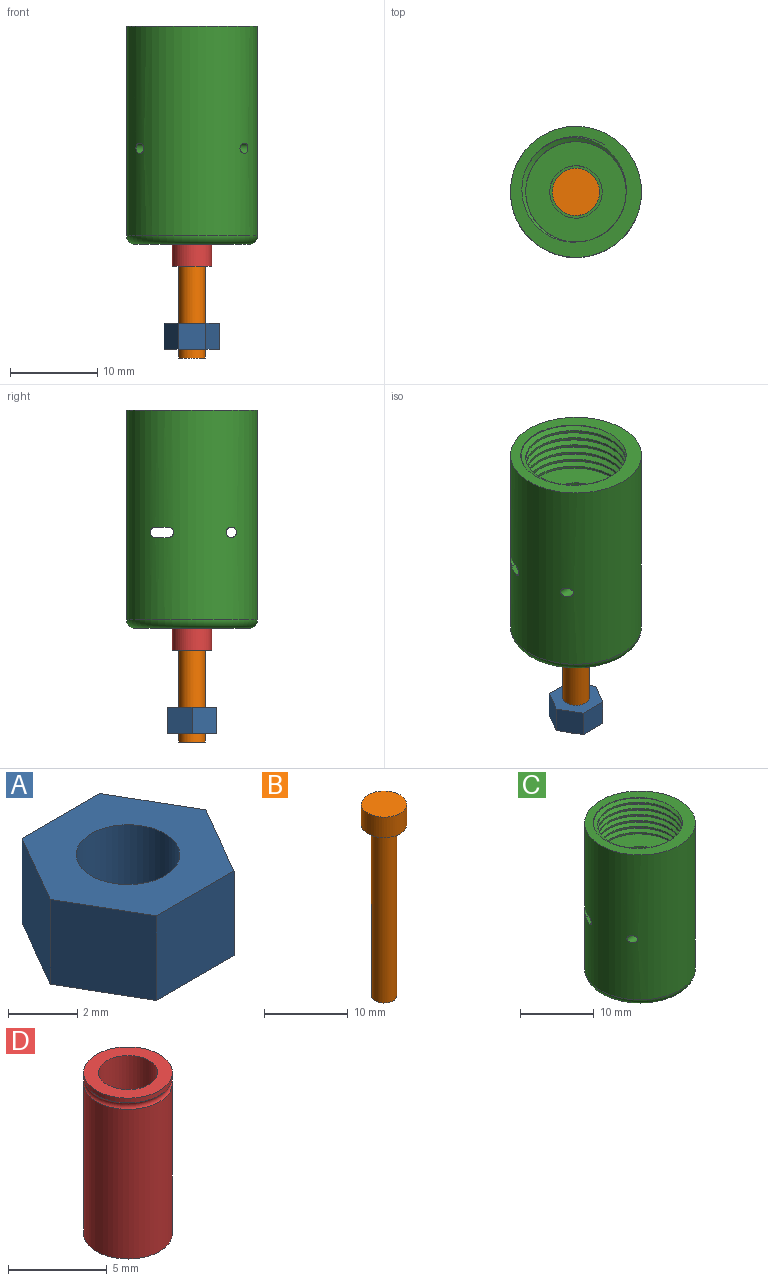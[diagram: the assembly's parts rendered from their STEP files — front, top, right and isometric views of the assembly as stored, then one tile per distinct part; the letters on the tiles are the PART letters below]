
ASSEMBLY  parts=4 mates=3
PART A: 9 faces, bbox 6.4x5.5x3 mm
  f0: plane 3x2.75mm, normal (0.87,0.5,0), area 9.5mm2, adj f1,f6,f7,f8
  f1: plane 3.18x3mm, normal (0,1,0), area 9.5mm2, adj f0,f2,f7,f8
  f2: plane 3x2.75mm, normal (-0.87,0.5,0), area 9.5mm2, adj f1,f3,f7,f8
  f3: plane 3x2.75mm, normal (-0.87,-0.5,0), area 9.5mm2, adj f2,f4,f7,f8
  f4: plane 3.18x3mm, normal (0,-1,0), area 9.5mm2, adj f3,f6,f7,f8
  f5: cylinder r=1.5mm len=3mm, axis (0,0,-1), area 28.3mm2, adj f7,f8
  f6: plane 3x2.75mm, normal (0.87,-0.5,0), area 9.5mm2, adj f0,f4,f7,f8
  f7: plane 6.35x5.5mm, normal (0,0,1), area 19.1mm2, adj f0,f1,f2,f3,f4,f5,f6
  f8: plane 6.35x5.5mm, normal (0,0,-1), area 19.1mm2, adj f0,f1,f2,f3,f4,f5,f6
PART B: 5 faces, bbox 5.4x5.4x28 mm
  f0: cylinder r=2.7mm len=5.4mm, axis (0,0,1), area 50.9mm2, adj f1,f2
  f1: plane 5.4x5.4mm, normal (0,0,-1), area 15.8mm2, adj f0,f3
  f2: plane 5.4x5.4mm, normal (0,0,1), area 22.9mm2, adj f0
  f3: cylinder r=1.5mm len=25mm, axis (0,0,1), area 235.6mm2, adj f1,f4
  f4: plane 3x3mm, normal (0,0,-1), area 7.1mm2, adj f3
PART C: 21 faces, bbox 16.6x16.6x25.7 mm
  f0: cylinder r=7.5mm len=24mm, axis (0,0,-1), area 1121.5mm2, adj f3,f12,f16,f17,f18,f19,f20
  f1: plane 6x6mm, normal (0,0,-1), area 8.6mm2, adj f11,f13
  f2: plane 12.27x12.27mm, normal (0,0,1), area 84.6mm2, adj f5,f6,f7,f8,f9
  f3: plane 15.32x15.32mm, normal (0,0,1), area 63.9mm2, adj f0,f5,f6,f7,f8
  f4: plane 13x13mm, normal (0,0,-1), area 94.2mm2, adj f12,f14
  f5: bspline ~14.53x12.58mm, area 141.9mm2, adj f2,f3,f7,f8
  f6: bspline ~14.53x12.58mm, area 142mm2, adj f2,f3,f7,f8
  f7: bspline ~14.63x12.67mm, area 34.5mm2, adj f2,f3,f5,f6
  f8: cylinder r=5.75mm len=11.5mm, axis (0,0,-1), area 56.4mm2, adj f2,f3,f5,f6
  f9: cylinder r=3mm len=7mm, axis (0,0,1), area 131.9mm2, adj f2,f10
  f10: plane 6x6mm, normal (0,0,1), area 8.6mm2, adj f9,f11
  f11: cylinder r=2.5mm len=12mm, axis (0,0,1), area 185.8mm2, adj f1,f10,f19
  f12: torus R=6.5mm, axis (0,0,1), area 70.4mm2, adj f0,f4
  f13: cylinder r=3mm len=6mm, axis (0,0,-1), area 9.4mm2, adj f1,f15
  f14: cylinder r=3.5mm len=7mm, axis (0,0,-1), area 11mm2, adj f4,f15
  f15: plane 7x7mm, normal (0,0,-1), area 10.2mm2, adj f13,f14
  f16: plane 13.99x1.5mm, normal (0,0,-1), area 19.9mm2, adj f0,f18,f19
  f17: plane 13.99x1.5mm, normal (0,0,1), area 19.9mm2, adj f0,f18,f19
  f18: cylinder r=0.6mm len=12.43mm, axis (1,0,0), area 23.4mm2, adj f0,f16,f17
  f19: cylinder r=0.6mm len=13.99mm, axis (1,0,0), area 23.2mm2, adj f0,f11,f16,f17
  f20: cylinder r=0.6mm len=12mm, axis (1,0,0), area 45.2mm2, adj f0
PART D: 6 faces, bbox 5.2x5.2x10 mm
  f0: cylinder r=2.25mm len=4.5mm, axis (0,0,-1), area 4.2mm2, adj f3,f5
  f1: cylinder r=1.5mm len=10mm, axis (0,0,-1), area 94.2mm2, adj f3,f4
  f2: cylinder r=2.25mm len=9.3mm, axis (0,0,-1), area 131.5mm2, adj f4,f5
  f3: plane 4.5x4.5mm, normal (0,0,1), area 8.8mm2, adj f0,f1
  f4: plane 4.5x4.5mm, normal (0,0,-1), area 8.8mm2, adj f1,f2
  f5: torus R=2.4mm, axis (0,0,1), area 6.4mm2, adj f0,f2
PLACE A t=(0,0,-12)mm
PLACE B rot(axis=(0,0,1),180deg) t=(0,0,15)mm
PLACE C at identity fixed
PLACE D t=(0,0,-2.5)mm
MATE fastened A.f5 <-> B.f3  axis (0,0,-1) through (0,0,-12)mm
MATE slider B.f0 <-> C.f9  axis (0,0,-1) through (0,0,12)mm
MATE fastened D.f0 <-> B.f0  axis (0,0,1) through (0,0,7.5)mm
